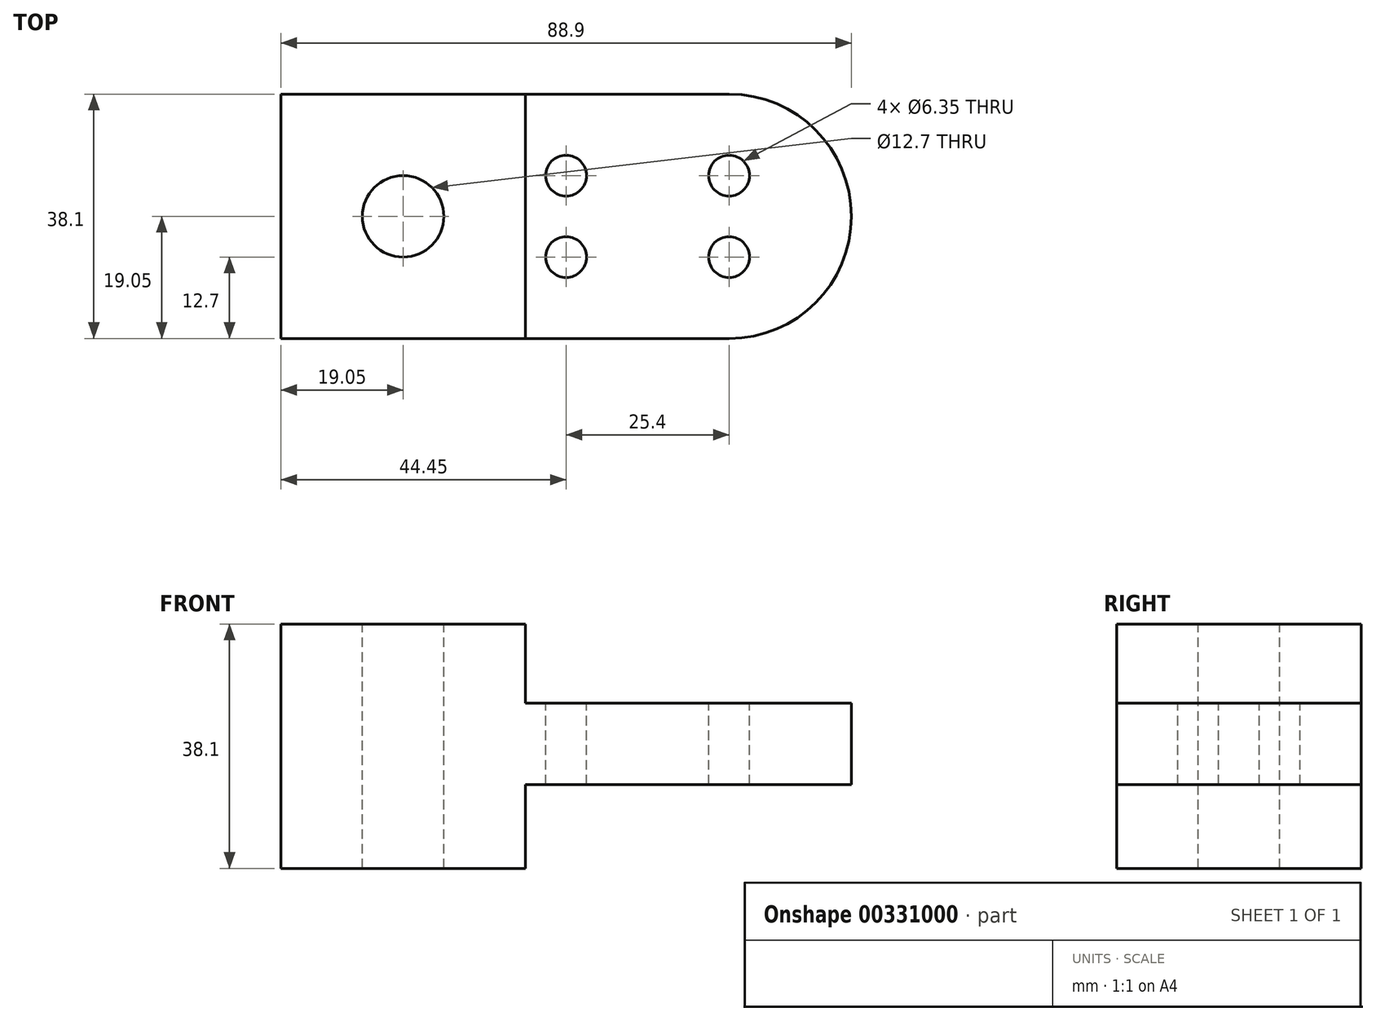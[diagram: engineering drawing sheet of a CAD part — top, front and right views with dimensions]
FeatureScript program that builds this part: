
annotation { "Feature Type Name" : "Feature", "Feature Type Description" : "" }
export const myFeature = defineFeature(function(context is Context, id is Id, definition is map)
    precondition{}
    {
        {
            var Q0;
            Q0=qCreatedBy(makeId("Front.planeOp"),FACE);
            var sketch = newSketch(context, id + "F0", { "sketchPlane" : qUnion([Q0])});
            skLineSegment(sketch, "E0", {"start": v(0, 0) * mm, "end": v(0, 38.1) * mm});
            skLineSegment(sketch, "E1", {"start": v(0, 38.1) * mm, "end": v(38.1, 38.1) * mm});
            skLineSegment(sketch, "E2", {"start": v(38.1, 38.1) * mm, "end": v(38.1, 0) * mm});
            skLineSegment(sketch, "E3", {"start": v(38.1, 0) * mm, "end": v(0, 0) * mm});
            skSolve(sketch);
        }
        {
            var Q0;
            Q0 = qSketchRegion(id + "F0", true);
            extrude(context, id + "F1", {"entities" : qUnion([Q0]), "depth" : 38.1 * mm});
        }
        {
            var Q0;
            Q0=makeQuery(id+"F1.opExtrude","CAP_FACE",FACE,{"disambiguationData":[OSD([sQuery(id+"F0.wireOp",EDGE,"E0"),sQuery(id+"F0.wireOp",EDGE,"E1"),sQuery(id+"F0.wireOp",EDGE,"E2"),sQuery(id+"F0.wireOp",EDGE,"E3")])],"isStart":false});
            var sketch = newSketch(context, id + "F2", { "sketchPlane" : qUnion([Q0])});
            skLineSegment(sketch, "E4.bottom", {"start": v(38.1, 25.79) * mm, "end": v(69.85, 25.79) * mm});
            skLineSegment(sketch, "E4.top", {"start": v(38.1, 13.09) * mm, "end": v(69.85, 13.09) * mm});
            skLineSegment(sketch, "E4.left", {"start": v(38.1, 25.79) * mm, "end": v(38.1, 13.09) * mm});
            skLineSegment(sketch, "E4.right", {"start": v(69.85, 25.79) * mm, "end": v(69.85, 13.09) * mm});
            skSolve(sketch);
        }
        {
            var Q0;
            Q0 = qSketchRegion(id + "F2", true);
            extrude(context, id + "F3", {"entities" : qUnion([Q0]), "operationType" : NewBodyOperationType.ADD, "oppositeDirection" : true, "depth" : 38.1 * mm});
        }
        {
            var Q0;
            Q0=makeQuery(id+"F3.opExtrude","SWEPT_FACE",FACE,{"disambiguationData":[OSD([sQuery(id+"F2.wireOp",EDGE,"E4.bottom")])]});
            var sketch = newSketch(context, id + "F4", { "sketchPlane" : qUnion([Q0])});
            skArc(sketch, "E5", {"start": v(69.85, -38.1) * mm, "mid": v(88.9, -19.05) * mm, "end": v(69.85, 0) * mm});
            skLineSegment(sketch, "E6", {"start": v(69.85, 0) * mm, "end": v(69.85, -38.1) * mm});
            skSolve(sketch);
        }
        {
            var Q0;
            Q0 = qSketchRegion(id + "F4", true);
            extrude(context, id + "F5", {"entities" : qUnion([Q0]), "operationType" : NewBodyOperationType.ADD, "oppositeDirection" : true, "depth" : 12.7 * mm});
        }
        {
            var Q0;
            Q0=makeQuery(id+"F1.opExtrude","SWEPT_FACE",FACE,{"disambiguationData":[OSD([sQuery(id+"F0.wireOp",EDGE,"E1")])]});
            var sketch = newSketch(context, id + "F6", { "sketchPlane" : qUnion([Q0])});
            skCircle(sketch, "E7", {"center": v(19.05, -19.05) * mm, "radius": 6.35 * mm});
            skCircle(sketch, "E8", {"center": v(44.45, -12.7) * mm, "radius": 3.18 * mm});
            skCircle(sketch, "E9", {"center": v(44.45, -25.4) * mm, "radius": 3.18 * mm});
            skCircle(sketch, "E10", {"center": v(69.85, -12.7) * mm, "radius": 3.18 * mm});
            skCircle(sketch, "E11", {"center": v(69.85, -25.4) * mm, "radius": 3.18 * mm});
            skSolve(sketch);
        }
        {
            var Q0;
            Q0 = qSketchRegion(id + "F6", true);
            extrude(context, id + "F7", {"entities" : qUnion([Q0]), "operationType" : NewBodyOperationType.REMOVE, "endBound" : BoundingType.THROUGH_ALL, "oppositeDirection" : true, "depth" : 25.4 * mm});
        }
    });
